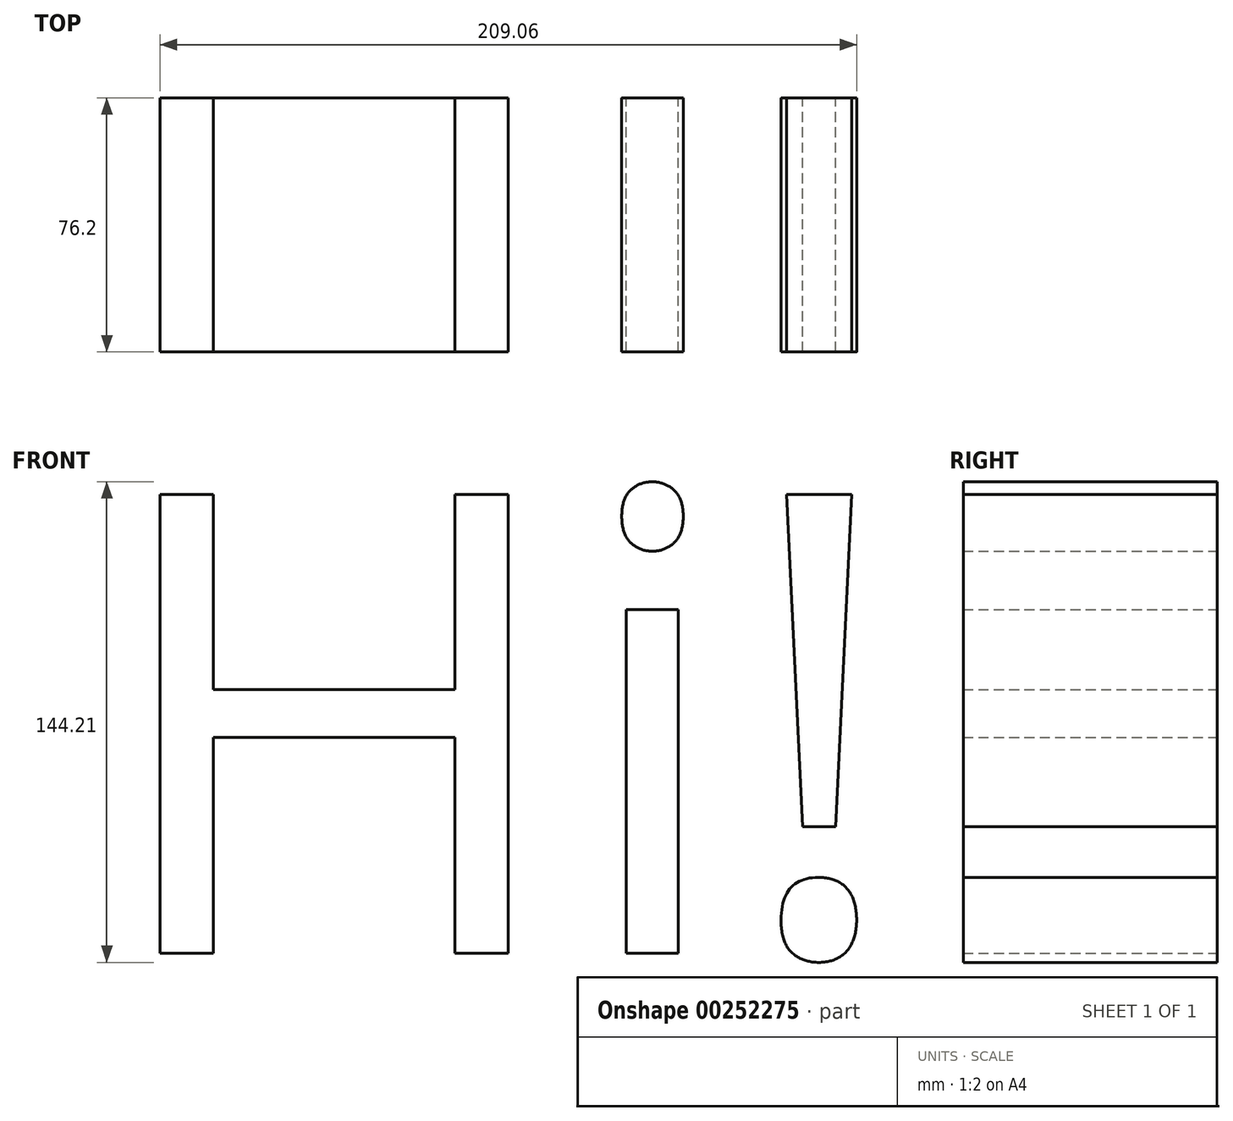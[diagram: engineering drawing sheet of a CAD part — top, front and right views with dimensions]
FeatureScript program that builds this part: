
annotation { "Feature Type Name" : "Feature", "Feature Type Description" : "" }
export const myFeature = defineFeature(function(context is Context, id is Id, definition is map)
    precondition{}
    {
        {
            var Q0;
            Q0=qCreatedBy(makeId("Front.planeOp"),FACE);
            var sketch = newSketch(context, id + "F0", { "sketchPlane" : qUnion([Q0])});
            skText(sketch, "E0", { "text": "Hi!\n", "fontName": "OpenSans-Regular.ttf"});
            const initialGuessF0  = {"E0": [-0.07196, -0.06454, 1, 0, 0.13879]};
            skSetInitialGuess(sketch, initialGuessF0);
            skSolve(sketch);
        }
        {
            var Q0;
            Q0 = qSketchRegion(id + "F0", true);
            extrude(context, id + "F1", {"entities" : qUnion([Q0]), "depth" : 76.2 * mm});
        }
    });
